# Revit family: Burko F-9500 Pendel
name_source: partatom
category: HLS-Bauteile
units: mm (PartAtom-declared; Revit-internal decimal feet)

## family parameters
Arbeitsebenenbasiert = Nein
Beim Laden mit Abzugskörper schneiden = Nein
Bemaßung runder Anschluss = Durchmesser verwenden
Beschriftungsausrichtung beibehalten = Nein
Gemeinsam genutzt = Nein
Immer vertikal = Ja
Klassifizierung = Keine
Raumberechnungspunkt = Nein
Teiletyp = Normal

## types (6) — shared parameters
Anschluss 1" = 25 mm  [stored 0.082021 ft]
Anschluss 1/2" = 15 mm  [stored 0.0492126 ft]
Datenblatt = https://www.burkhalter-h2o.ch
Homepage = https://www.burkhalter-h2o.ch
LUT = LUT_Burko_F-9500
Sockel_Höhe = 100 mm  [stored 0.328084 ft]
Steuerung_Breite = 175 mm  [stored 0.574147 ft]
Steuerung_Höhe = 215 mm
Steuerung_Tiefe = 75 mm  [stored 0.246063 ft]
zero-valued in all types: Vorgabe-Ansicht

## per-type parameters (varying)
| type | A | B | Behälterkopf | C | G | Harzinhalt_pro_Harzdruckbehälter | Sockel_Absatz_Oben | Sockel_Absatz_Unten |
| Burko F-9500 - 50L | 305 mm | 1300 mm | 75 mm  [stored 0.246063 ft] | 1430 mm | 500 mm | 50L | 133 mm | 163 mm |
| Burko F-9500 - 75L | 369 mm  [stored 1.21063 ft] | 1720 mm | 100 mm  [stored 0.328084 ft] | 1850 mm | 500 mm | 75L | 165 mm  [stored 0.541339 ft] | 195 mm  [stored 0.639764 ft] |
| Burko F-9500 - 100L | 406 mm  [stored 1.33202 ft] | 1720 mm | 125 mm  [stored 0.410105 ft] | 1850 mm | 605 mm | 100L | 183 mm | 213 mm |
| Burko F-9500 - 125L | 406 mm  [stored 1.33202 ft] | 1720 mm | 125 mm  [stored 0.410105 ft] | 1850 mm | 605 mm | 125L | 183 mm | 213 mm |
| Burko F-9500 - 150L | 552 mm  [stored 1.81102 ft] | 1690 mm  [stored 5.54462 ft] | 175 mm  [stored 0.574147 ft] | 1820 mm  [stored 5.97113 ft] | 705 mm | 150L | 256 mm  [stored 0.839895 ft] | 286 mm |
| Burko F-9500 - 200L | 552 mm  [stored 1.81102 ft] | 1690 mm  [stored 5.54462 ft] | 175 mm  [stored 0.574147 ft] | 1820 mm  [stored 5.97113 ft] | 705 mm | 200L | 256 mm  [stored 0.839895 ft] | 286 mm |

note: [stored X ft] marks values corroborated as IEEE doubles in the binary element streams (Revit-internal decimal feet)
